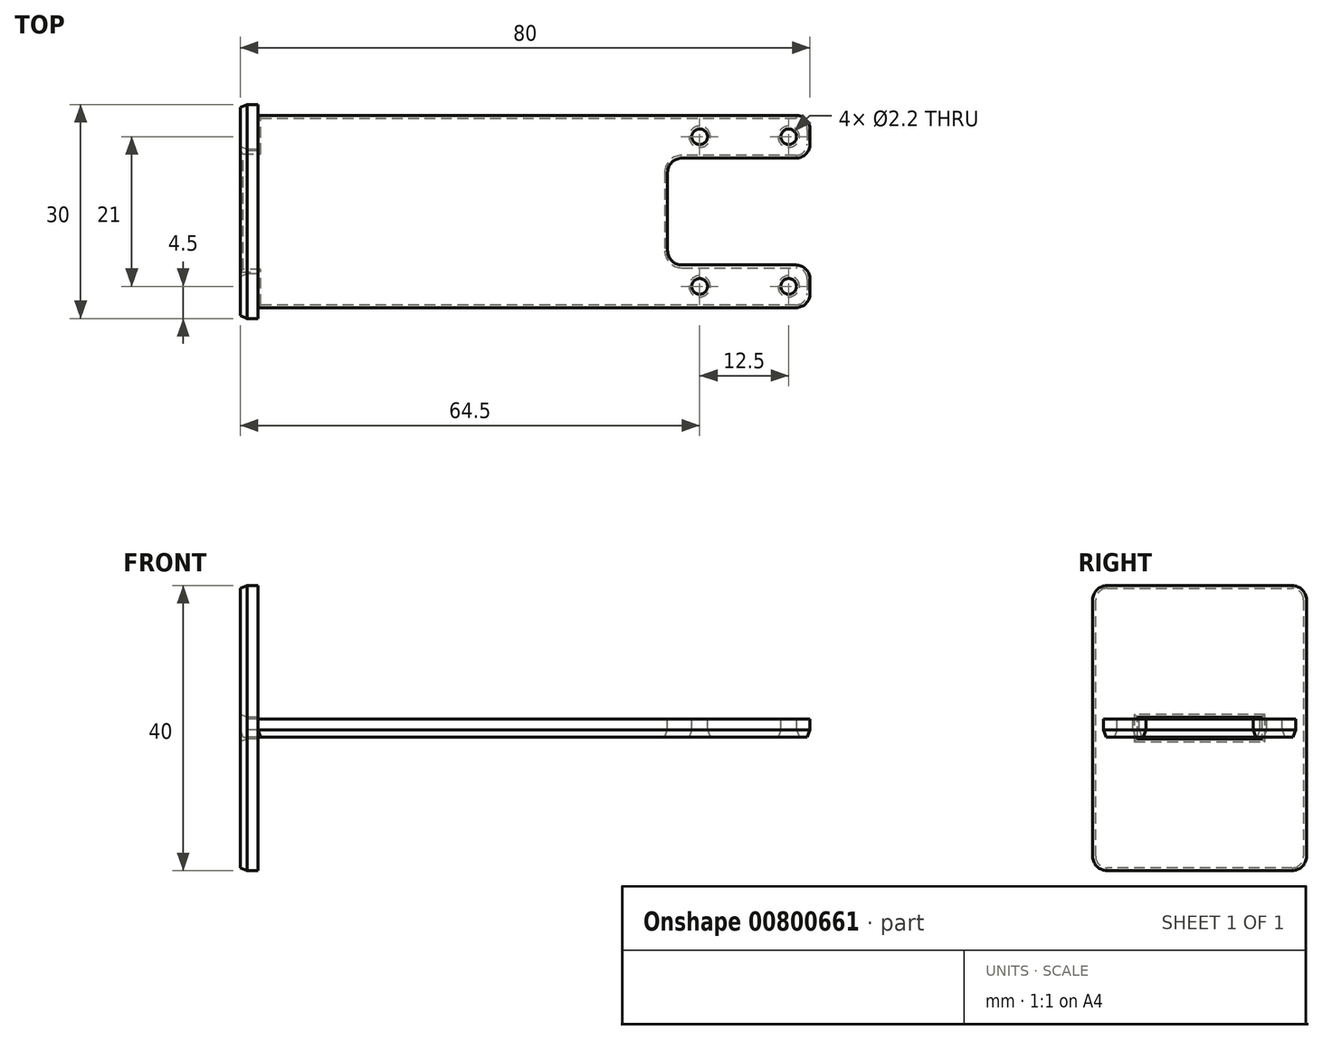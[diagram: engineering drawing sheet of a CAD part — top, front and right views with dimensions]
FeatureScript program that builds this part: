
annotation { "Feature Type Name" : "Feature", "Feature Type Description" : "" }
export const myFeature = defineFeature(function(context is Context, id is Id, definition is map)
    precondition{}
    {
        {
            var Q0;
            Q0=qCreatedBy(makeId("Top.planeOp"),FACE);
            var sketch = newSketch(context, id + "F0", { "sketchPlane" : qUnion([Q0])});
            skLineSegment(sketch, "E0.bottom", {"start": v(-60, -1) * mm, "end": v(15.5, -1) * mm});
            skLineSegment(sketch, "E0.top", {"start": v(-60, 26) * mm, "end": v(15.5, 26) * mm});
            skLineSegment(sketch, "E0.left", {"start": v(-62.5, 4) * mm, "end": v(-62.5, 21) * mm});
            skLineSegment(sketch, "E1", {"start": v(15.5, 20) * mm, "end": v(-0.5, 20) * mm});
            skLineSegment(sketch, "E2", {"start": v(-2.5, 18) * mm, "end": v(-2.5, 7) * mm});
            skLineSegment(sketch, "E3", {"start": v(-0.5, 5) * mm, "end": v(15.5, 5) * mm});
            skCircle(sketch, "E4", {"center": v(2, 2) * mm, "radius": 1.1 * mm});
            skCircle(sketch, "E5", {"center": v(2, 23) * mm, "radius": 1.1 * mm});
            skCircle(sketch, "E6", {"center": v(14.5, 23) * mm, "radius": 1.1 * mm});
            skCircle(sketch, "E7", {"center": v(14.5, 2) * mm, "radius": 1.1 * mm});
            skLineSegment(sketch, "E8", {"start": v(17.5, 24) * mm, "end": v(17.5, 22) * mm});
            skLineSegment(sketch, "E9", {"start": v(17.5, 3) * mm, "end": v(17.5, 1) * mm});
            skPoint(sketch, "E10.visualSharp", {"position": v(17.5, 26) * mm});
            skArc(sketch, "E10.filletArc", {"start": v(17.5, 24) * mm, "mid": v(16.91, 25.41) * mm, "end": v(15.5, 26) * mm});
            skPoint(sketch, "E11.visualSharp", {"position": v(17.5, 20) * mm});
            skArc(sketch, "E11.filletArc", {"start": v(15.5, 20) * mm, "mid": v(16.91, 20.59) * mm, "end": v(17.5, 22) * mm});
            skPoint(sketch, "E12.visualSharp", {"position": v(17.5, 5) * mm});
            skArc(sketch, "E12.filletArc", {"start": v(17.5, 3) * mm, "mid": v(16.91, 4.41) * mm, "end": v(15.5, 5) * mm});
            skPoint(sketch, "E13.visualSharp", {"position": v(17.5, -1) * mm});
            skArc(sketch, "E13.filletArc", {"start": v(15.5, -1) * mm, "mid": v(16.91, -0.41) * mm, "end": v(17.5, 1) * mm});
            skPoint(sketch, "E14.visualSharp", {"position": v(-2.5, 5) * mm});
            skArc(sketch, "E14.filletArc", {"start": v(-2.5, 7) * mm, "mid": v(-1.91, 5.59) * mm, "end": v(-0.5, 5) * mm});
            skPoint(sketch, "E15.visualSharp", {"position": v(-2.5, 20) * mm});
            skArc(sketch, "E15.filletArc", {"start": v(-0.5, 20) * mm, "mid": v(-1.91, 19.41) * mm, "end": v(-2.5, 18) * mm});
            skLineSegment(sketch, "E16", {"start": v(-60, 26) * mm, "end": v(-60, 21) * mm});
            skLineSegment(sketch, "E17", {"start": v(-60, 21) * mm, "end": v(-62.5, 21) * mm});
            skLineSegment(sketch, "E18", {"start": v(-60, -1) * mm, "end": v(-60, 4) * mm});
            skLineSegment(sketch, "E19", {"start": v(-60, 4) * mm, "end": v(-62.5, 4) * mm});
            skSolve(sketch);
        }
        {
            var Q0;
            Q0=makeQuery(id+"F0.imprint","IMPRINT",FACE,{"disambiguationData":[TD([[makeQuery(id+"F0.imprint","IMPRINT",EDGE,{"derivedFrom":sQuery(id+"F0.wireOp",EDGE,"E0.bottom")}),1.0]])]});
            extrude(context, id + "F1", {"entities" : qUnion([Q0]), "oppositeDirection" : true, "depth" : 2.5 * mm, "offsetDistance" : 25 * mm});
        }
        {
            var Q0;
            Q0=makeQuery(id+"F1.opExtrude","SWEPT_FACE",FACE,{"disambiguationData":[OSD([sQuery(id+"F0.wireOp",EDGE,"E0.left")])]});
            var sketch = newSketch(context, id + "F2", { "sketchPlane" : qUnion([Q0])});
            skLineSegment(sketch, "E20.bottom", {"start": v(-25.5, 18.75) * mm, "end": v(0.5, 18.75) * mm});
            skLineSegment(sketch, "E20.top", {"start": v(-25.5, -21.25) * mm, "end": v(0.5, -21.25) * mm});
            skLineSegment(sketch, "E20.left", {"start": v(-27.5, 16.75) * mm, "end": v(-27.5, -19.25) * mm});
            skLineSegment(sketch, "E20.right", {"start": v(2.5, 16.75) * mm, "end": v(2.5, -19.25) * mm});
            skLineSegment(sketch, "E21.0", {"start": v(-3.75, 0.25) * mm, "end": v(-21.25, 0.25) * mm});
            skLineSegment(sketch, "E21.1", {"start": v(-3.75, -2.75) * mm, "end": v(-3.75, 0.25) * mm});
            skLineSegment(sketch, "E21.2", {"start": v(-21.25, -2.75) * mm, "end": v(-3.75, -2.75) * mm});
            skLineSegment(sketch, "E21.3", {"start": v(-21.25, 0.25) * mm, "end": v(-21.25, -2.75) * mm});
            skPoint(sketch, "E22.0", {"position": v(-21, -1.25) * mm});
            skPoint(sketch, "E23.0", {"position": v(-4, -1.25) * mm});
            skLineSegment(sketch, "E24", {"start": v(-21, -1.25) * mm, "end": v(-4, -1.25) * mm, "construction": true});
            skLineSegment(sketch, "E25", {"start": v(-12.5, 18.75) * mm, "end": v(-12.5, -21.25) * mm, "construction": true});
            skPoint(sketch, "E26", {"position": v(-12.5, -1.25) * mm});
            skPoint(sketch, "E27.visualSharp", {"position": v(2.5, 18.75) * mm});
            skArc(sketch, "E27.filletArc", {"start": v(2.5, 16.75) * mm, "mid": v(1.91, 18.16) * mm, "end": v(0.5, 18.75) * mm});
            skPoint(sketch, "E28.visualSharp", {"position": v(2.5, -21.25) * mm});
            skArc(sketch, "E28.filletArc", {"start": v(0.5, -21.25) * mm, "mid": v(1.91, -20.66) * mm, "end": v(2.5, -19.25) * mm});
            skPoint(sketch, "E29.visualSharp", {"position": v(-27.5, -21.25) * mm});
            skArc(sketch, "E29.filletArc", {"start": v(-27.5, -19.25) * mm, "mid": v(-26.91, -20.66) * mm, "end": v(-25.5, -21.25) * mm});
            skPoint(sketch, "E30.visualSharp", {"position": v(-27.5, 18.75) * mm});
            skArc(sketch, "E30.filletArc", {"start": v(-25.5, 18.75) * mm, "mid": v(-26.91, 18.16) * mm, "end": v(-27.5, 16.75) * mm});
            skSolve(sketch);
        }
        {
            var Q0;
            {var subQ3=sQuery(id+"F2.wireOp",EDGE,"E20.bottom");Q0=makeQuery(id+"F2.imprint","IMPRINT",FACE,{"disambiguationData":[TD([[makeQuery(id+"F2.imprint","IMPRINT",EDGE,{"derivedFrom":subQ3}),-1.0]])]});}
            var Q1;
            Q1=makeQuery(id+"F1.opExtrude","SWEPT_FACE",FACE,{"disambiguationData":[OSD([sQuery(id+"F0.wireOp",EDGE,"E18")])]});
            extrude(context, id + "F3", {"entities" : qUnion([Q0]), "endBound" : BoundingType.UP_TO_SURFACE, "oppositeDirection" : true, "depth" : 25 * mm, "endBoundEntityFace" : qUnion([Q1]), "offsetDistance" : 25 * mm});
        }
        {
            var Q0;
            Q0=makeQuery(id+"F3.opExtrude","CAP_FACE",FACE,{"disambiguationData":[OSD([sQuery(id+"F2.wireOp",EDGE,"E20.bottom"),sQuery(id+"F2.wireOp",EDGE,"E20.top"),sQuery(id+"F2.wireOp",EDGE,"E20.left"),sQuery(id+"F2.wireOp",EDGE,"E20.right"),sQuery(id+"F2.wireOp",EDGE,"E21.0"),sQuery(id+"F2.wireOp",EDGE,"E21.1"),sQuery(id+"F2.wireOp",EDGE,"E21.2"),sQuery(id+"F2.wireOp",EDGE,"E21.3"),sQuery(id+"F2.wireOp",EDGE,"E27.filletArc"),sQuery(id+"F2.wireOp",EDGE,"E28.filletArc"),sQuery(id+"F2.wireOp",EDGE,"E29.filletArc"),sQuery(id+"F2.wireOp",EDGE,"E30.filletArc")])],"isStart":true});
            chamfer(context, id + "F4", {"entities" : qUnion([Q0]), "chamferType" : ChamferType.TWO_OFFSETS, "width1" : 1 * mm, "oppositeDirection" : false, "width2" : .4 * mm, "tangentPropagation" : true});
        }
        {
            var Q0;
            Q0=makeQuery(id+"F1.opExtrude","CAP_FACE",FACE,{"disambiguationData":[OSD([sQuery(id+"F0.wireOp",EDGE,"E0.bottom"),sQuery(id+"F0.wireOp",EDGE,"E0.top"),sQuery(id+"F0.wireOp",EDGE,"E0.left"),sQuery(id+"F0.wireOp",EDGE,"E1"),sQuery(id+"F0.wireOp",EDGE,"E2"),sQuery(id+"F0.wireOp",EDGE,"E3"),sQuery(id+"F0.wireOp",EDGE,"E4"),sQuery(id+"F0.wireOp",EDGE,"E5"),sQuery(id+"F0.wireOp",EDGE,"E6"),sQuery(id+"F0.wireOp",EDGE,"E7"),sQuery(id+"F0.wireOp",EDGE,"E8"),sQuery(id+"F0.wireOp",EDGE,"E9"),sQuery(id+"F0.wireOp",EDGE,"E10.filletArc"),sQuery(id+"F0.wireOp",EDGE,"E11.filletArc"),sQuery(id+"F0.wireOp",EDGE,"E12.filletArc"),sQuery(id+"F0.wireOp",EDGE,"E13.filletArc"),sQuery(id+"F0.wireOp",EDGE,"E14.filletArc"),sQuery(id+"F0.wireOp",EDGE,"E15.filletArc"),sQuery(id+"F0.wireOp",EDGE,"E16"),sQuery(id+"F0.wireOp",EDGE,"E17"),sQuery(id+"F0.wireOp",EDGE,"E18"),sQuery(id+"F0.wireOp",EDGE,"E19")])],"isStart":false});
            chamfer(context, id + "F5", {"entities" : qUnion([Q0]), "chamferType" : ChamferType.TWO_OFFSETS, "width1" : 1 * mm, "oppositeDirection" : false, "width2" : .4 * mm, "tangentPropagation" : true});
        }
    });
